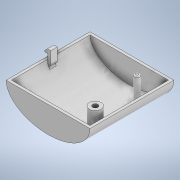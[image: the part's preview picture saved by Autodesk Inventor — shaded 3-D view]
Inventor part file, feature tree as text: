
AUTODESK INVENTOR PART (.ipt)
format: ipt  version: 2021 (Build 250183000, 183)  size: 245,760 bytes
history: native  units: mm
features: sketch x9, extrude x8, fillet x2, other x1, shell x1, plane x1, hole x1, thread x1
ambient origin geometry x8: Origin, YZ Plane, XZ Plane, XY Plane, X Axis, Y Axis, Z Axis, Center Point
bodies: Body1 (feature_tree)
feature tree (24):
  other  "Sólido1"
  sketch  "Boceto1"  dims[d0=2.5mm d2=3.0mm d3=4.0mm]
  extrude  "Extrusión1"  Depth=3.0mm
  shell  "Vaciado1"  Thickness=4.0mm
  plane  "Plano de trabajo2"
  extrude  "Extrusión2"  Depth=2.0mm
  extrude  "Extrusión3"  Depth=30.0mm
  extrude  "Extrusión4"  Depth=20.0mm TaperAngle=0.0deg
  extrude  "Extrusión5"  Depth=2.0mm TaperAngle=0.0deg
  fillet  "Empalme1"  [1 undecoded]
  extrude  "Extrusión6"  Depth=10.0mm
  hole  "Agujero1"  [1 undecoded]
  thread  "Rosca1"  [1 undecoded]
  extrude  "Extrusión7"  Depth=30.0mm
  extrude  "Extrusión8"  Depth=2.0mm
  fillet  "Empalme2"  Radius=1.0mm
  sketch  "Boceto2"  dims[d4=4.0mm d6=2.0mm]
  sketch  "Boceto3"  dims[d7=30.0mm d8=64.0mm]
  sketch  "Boceto4"  dims[d9=64.0mm d10=20.0mm d11=0.0mm]
  sketch  "Boceto5"  dims[d12=2.0mm d13=20.0mm d14=0.0mm d19=-20.0mm]
  sketch  "Boceto6"  dims[d20=10.0mm d21=16.0mm]
  sketch  "Boceto7"  dims[d22=16.0mm d23=4.0mm d24=9.0mm]
  sketch  "Boceto8"  dims[d25=30.0mm d26=0.0mm d27=0.25mm]
  sketch  "Boceto9"  dims[d28=45.0deg d29=2.0mm d30=1.0mm d31=3.0mm d32=45.0deg d33=2.0mm d34=5.0mm d35=4.0mm d36=0.0mm d37=0.0mm d38=5.0mm d39=0.0mm d40=4.0mm d41=6.0mm d42=0.0mm d43=1.0mm d44=9.0mm d45=1.0mm d46=0.0mm d47=4.0mm d48=4.0mm d49=6.0mm d50=4.0mm d51=2.0mm d52=90.0deg d53=10.0mm d54=0.0mm d55=10.0mm d56=0.0mm d59=20.0mm d60=15.0mm d61=1.0mm d62=0.0mm d63=20.0mm d65=0.0mm d66=0.0mm d67=2.0mm]
note: 3 required parameter values undecoded (feature->parameter linkage not recoverable at this tier; creation-order binding heuristic only, values carry confidence <= 0.55)
